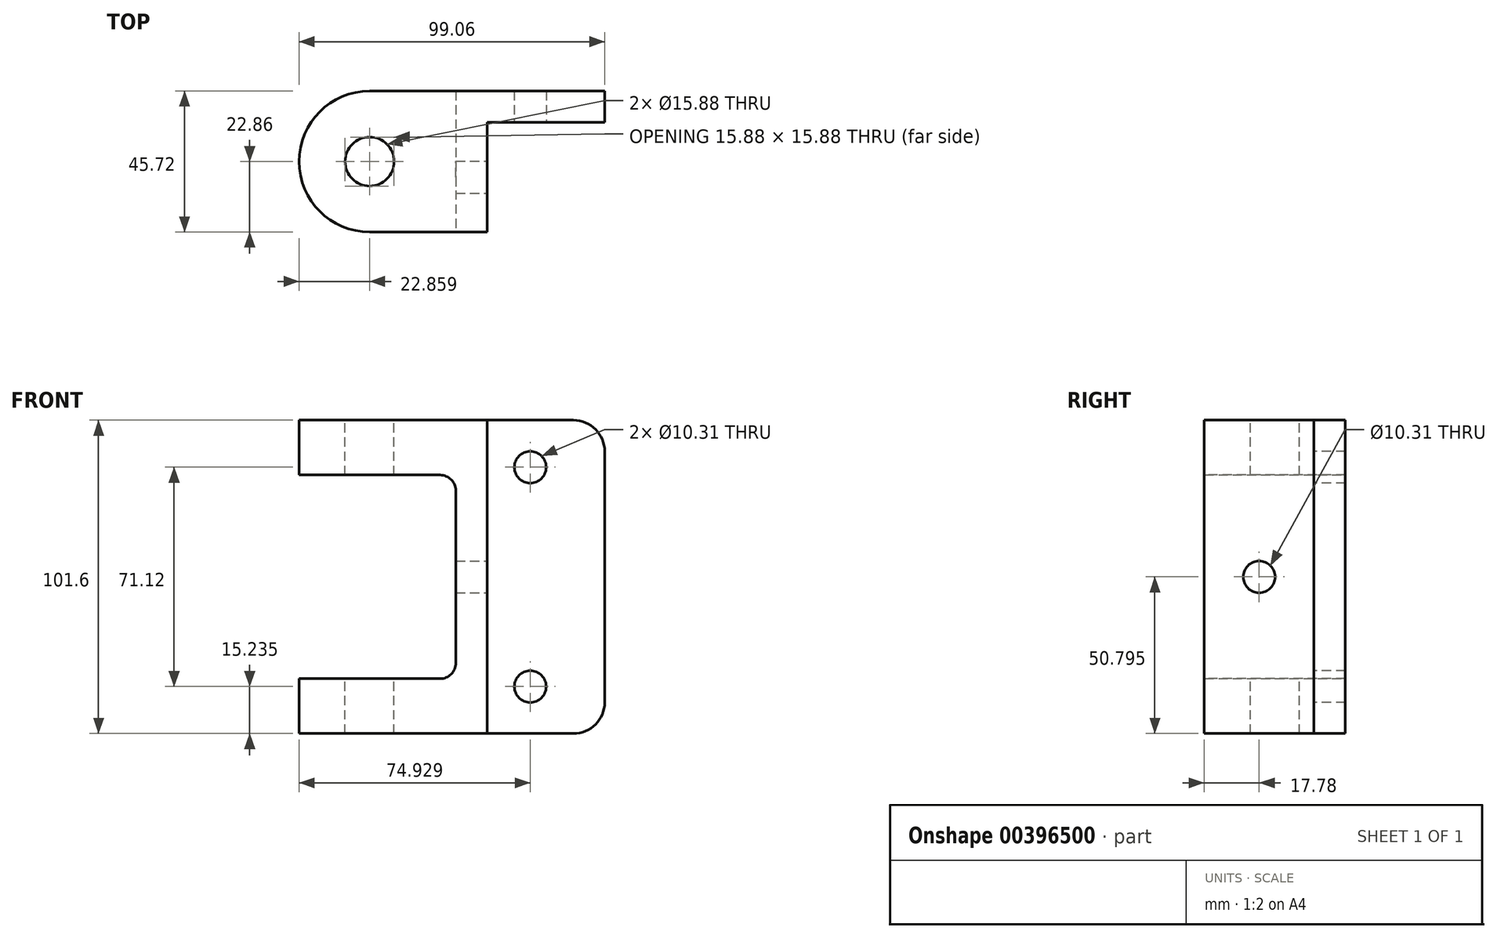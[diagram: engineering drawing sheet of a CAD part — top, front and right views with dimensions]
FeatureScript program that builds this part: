
annotation { "Feature Type Name" : "Feature", "Feature Type Description" : "" }
export const myFeature = defineFeature(function(context is Context, id is Id, definition is map)
    precondition{}
    {
        {
            var Q0;
            Q0=qCreatedBy(makeId("Front.planeOp"),FACE);
            var sketch = newSketch(context, id + "F0", { "sketchPlane" : qUnion([Q0])});
            skLineSegment(sketch, "E0.bottom", {"start": v(-44.01, 40.62) * mm, "end": v(55.05, 40.62) * mm});
            skLineSegment(sketch, "E0.top", {"start": v(-44.01, -60.98) * mm, "end": v(55.05, -60.98) * mm});
            skLineSegment(sketch, "E0.left", {"start": v(-44.01, 40.62) * mm, "end": v(-44.01, -60.98) * mm});
            skLineSegment(sketch, "E0.right", {"start": v(55.05, 40.62) * mm, "end": v(55.05, -60.98) * mm});
            skSolve(sketch);
        }
        {
            var Q0;
            Q0=makeQuery(id+"F0.imprint","IMPRINT",FACE,{"disambiguationData":[TD([[makeQuery(id+"F0.imprint","IMPRINT",EDGE,{"derivedFrom":sQuery(id+"F0.wireOp",EDGE,"E0.bottom")}),-1.0]])]});
            extrude(context, id + "F1", {"entities" : qUnion([Q0]), "depth" : 45.72 * mm});
        }
        {
            var Q0;
            Q0=makeQuery(id+"F1.opExtrude","CAP_FACE",FACE,{"disambiguationData":[OSD([sQuery(id+"F0.wireOp",EDGE,"E0.bottom"),sQuery(id+"F0.wireOp",EDGE,"E0.top"),sQuery(id+"F0.wireOp",EDGE,"E0.left"),sQuery(id+"F0.wireOp",EDGE,"E0.right")])],"isStart":false});
            var sketch = newSketch(context, id + "F2", { "sketchPlane" : qUnion([Q0])});
            skLineSegment(sketch, "E1.bottom", {"start": v(16.95, 43.76) * mm, "end": v(62.8, 43.76) * mm});
            skLineSegment(sketch, "E1.top", {"start": v(16.95, -63.37) * mm, "end": v(62.8, -63.37) * mm});
            skLineSegment(sketch, "E1.left", {"start": v(16.95, 43.76) * mm, "end": v(16.95, -63.37) * mm});
            skLineSegment(sketch, "E1.right", {"start": v(62.8, 43.76) * mm, "end": v(62.8, -63.37) * mm});
            skSolve(sketch);
        }
        {
            var Q0;
            Q0 = qSketchRegion(id + "F2", true);
            extrude(context, id + "F3", {"entities" : qUnion([Q0]), "operationType" : NewBodyOperationType.REMOVE, "oppositeDirection" : true, "depth" : 35.56 * mm});
        }
        {
            var Q0;
            Q0=makeQuery(id+"F1.opExtrude","CAP_FACE",FACE,{"disambiguationData":[OSD([sQuery(id+"F0.wireOp",EDGE,"E0.bottom"),sQuery(id+"F0.wireOp",EDGE,"E0.top"),sQuery(id+"F0.wireOp",EDGE,"E0.left"),sQuery(id+"F0.wireOp",EDGE,"E0.right")])],"isStart":false});
            var sketch = newSketch(context, id + "F4", { "sketchPlane" : qUnion([Q0])});
            skLineSegment(sketch, "E2.bottom", {"start": v(-89.68, 22.84) * mm, "end": v(6.79, 22.84) * mm});
            skLineSegment(sketch, "E2.top", {"start": v(-89.68, -43.2) * mm, "end": v(6.79, -43.2) * mm});
            skLineSegment(sketch, "E2.left", {"start": v(-89.68, 22.84) * mm, "end": v(-89.68, -43.2) * mm});
            skLineSegment(sketch, "E2.right", {"start": v(6.79, 22.84) * mm, "end": v(6.79, -43.2) * mm});
            skSolve(sketch);
        }
        {
            var Q0;
            Q0 = qSketchRegion(id + "F4", true);
            extrude(context, id + "F5", {"entities" : qUnion([Q0]), "operationType" : NewBodyOperationType.REMOVE, "endBound" : BoundingType.THROUGH_ALL, "oppositeDirection" : true, "depth" : 25.4 * mm});
        }
        {
            var Q0;
            {var subQ0=sQuery(id+"F0.wireOp",EDGE,"E0.bottom");var subQ1=sQuery(id+"F0.wireOp",EDGE,"E0.left");Q0=makeQuery(id+"F5.boolean.opBoolean","SPLIT",EDGE,{"disambiguationData":[TD([makeQuery(id+"F1.opExtrude","SWEPT_FACE",FACE,{"disambiguationData":[OSD([subQ0])]})])],"derivedFrom":makeQuery(id+"F1.opExtrude","CAP_EDGE",EDGE,{"disambiguationData":[OSD([subQ1])],"isStart":true})});}
            var Q1;
            {var subQ0=sQuery(id+"F0.wireOp",EDGE,"E0.bottom");var subQ1=sQuery(id+"F0.wireOp",EDGE,"E0.left");Q1=makeQuery(id+"F5.boolean.opBoolean","SPLIT",EDGE,{"disambiguationData":[TD([makeQuery(id+"F1.opExtrude","SWEPT_FACE",FACE,{"disambiguationData":[OSD([subQ0])]})])],"derivedFrom":makeQuery(id+"F1.opExtrude","CAP_EDGE",EDGE,{"disambiguationData":[OSD([subQ1])],"isStart":false})});}
            var Q2;
            {var subQ0=sQuery(id+"F0.wireOp",EDGE,"E0.left");var subQ1=sQuery(id+"F0.wireOp",EDGE,"E0.top");Q2=makeQuery(id+"F5.boolean.opBoolean","SPLIT",EDGE,{"disambiguationData":[TD([makeQuery(id+"F1.opExtrude","SWEPT_FACE",FACE,{"disambiguationData":[OSD([subQ1])]})])],"derivedFrom":makeQuery(id+"F1.opExtrude","CAP_EDGE",EDGE,{"disambiguationData":[OSD([subQ0])],"isStart":true})});}
            var Q3;
            {var subQ0=sQuery(id+"F0.wireOp",EDGE,"E0.left");var subQ1=sQuery(id+"F0.wireOp",EDGE,"E0.top");Q3=makeQuery(id+"F5.boolean.opBoolean","SPLIT",EDGE,{"disambiguationData":[TD([makeQuery(id+"F1.opExtrude","SWEPT_FACE",FACE,{"disambiguationData":[OSD([subQ1])]})])],"derivedFrom":makeQuery(id+"F1.opExtrude","CAP_EDGE",EDGE,{"disambiguationData":[OSD([subQ0])],"isStart":false})});}
            fillet(context, id + "F6", {"entities" : qUnion([Q0, Q1, Q2, Q3]), "radius" : 22.86 * mm, "tangentPropagation" : true, "allowEdgeOverflow" : false});
        }
        {
            var Q0;
            Q0=makeQuery(id+"F1.opExtrude","SWEPT_FACE",FACE,{"disambiguationData":[OSD([sQuery(id+"F0.wireOp",EDGE,"E0.bottom")])]});
            var sketch = newSketch(context, id + "F7", { "sketchPlane" : qUnion([Q0])});
            skCircle(sketch, "E3", {"center": v(-21.15, -22.86) * mm, "radius": 7.94 * mm});
            skSolve(sketch);
        }
        {
            var Q0;
            Q0 = qSketchRegion(id + "F7", true);
            extrude(context, id + "F8", {"entities" : qUnion([Q0]), "operationType" : NewBodyOperationType.REMOVE, "endBound" : BoundingType.THROUGH_ALL, "oppositeDirection" : true, "depth" : 25.4 * mm});
        }
        {
            var Q0;
            Q0=makeQuery(id+"F5.boolean.opBoolean","COPY",EDGE,{"derivedFrom":makeQuery(id+"F5.opExtrude","SWEPT_EDGE",EDGE,{"disambiguationData":[OSD([sQuery(id+"F4.wireOp",EDGE,"E2.bottom"),sQuery(id+"F4.wireOp",EDGE,"E2.right")])]})});
            var Q1;
            Q1=makeQuery(id+"F5.boolean.opBoolean","COPY",EDGE,{"derivedFrom":makeQuery(id+"F5.opExtrude","SWEPT_EDGE",EDGE,{"disambiguationData":[OSD([sQuery(id+"F4.wireOp",EDGE,"E2.top"),sQuery(id+"F4.wireOp",EDGE,"E2.right")])]})});
            fillet(context, id + "F9", {"entities" : qUnion([Q0, Q1]), "radius" : 5.08 * mm, "tangentPropagation" : true, "allowEdgeOverflow" : false});
        }
        {
            var Q0;
            Q0=makeQuery(id+"F1.opExtrude","SWEPT_EDGE",EDGE,{"disambiguationData":[OSD([sQuery(id+"F0.wireOp",EDGE,"E0.bottom"),sQuery(id+"F0.wireOp",EDGE,"E0.right")])]});
            var Q1;
            Q1=makeQuery(id+"F1.opExtrude","SWEPT_EDGE",EDGE,{"disambiguationData":[OSD([sQuery(id+"F0.wireOp",EDGE,"E0.top"),sQuery(id+"F0.wireOp",EDGE,"E0.right")])]});
            fillet(context, id + "F10", {"entities" : qUnion([Q0, Q1]), "radius" : 10.16 * mm, "tangentPropagation" : true, "allowEdgeOverflow" : false});
        }
        {
            var Q0;
            Q0=makeQuery(id+"F3.boolean.opBoolean","COPY",FACE,{"derivedFrom":makeQuery(id+"F3.opExtrude","SWEPT_FACE",FACE,{"disambiguationData":[OSD([sQuery(id+"F2.wireOp",EDGE,"E1.left")])]})});
            var sketch = newSketch(context, id + "F11", { "sketchPlane" : qUnion([Q0])});
            skCircle(sketch, "E4", {"center": v(-27.94, -10.18) * mm, "radius": 5.16 * mm});
            skPoint(sketch, "E4.centerSnap0", {"position": v(-27.94, 40.62) * mm});
            skPoint(sketch, "E4.centerSnap1", {"position": v(-45.72, -10.18) * mm});
            skSolve(sketch);
        }
        {
            var Q0;
            Q0 = qSketchRegion(id + "F11", true);
            extrude(context, id + "F12", {"entities" : qUnion([Q0]), "operationType" : NewBodyOperationType.REMOVE, "endBound" : BoundingType.THROUGH_ALL, "oppositeDirection" : true, "depth" : 25.4 * mm});
        }
        {
            var Q0;
            Q0=makeQuery(id+"F3.boolean.opBoolean","COPY",FACE,{"derivedFrom":makeQuery(id+"F3.opExtrude","CAP_FACE",FACE,{"disambiguationData":[OSD([sQuery(id+"F2.wireOp",EDGE,"E1.bottom"),sQuery(id+"F2.wireOp",EDGE,"E1.top"),sQuery(id+"F2.wireOp",EDGE,"E1.left"),sQuery(id+"F2.wireOp",EDGE,"E1.right")])],"isStart":false})});
            var sketch = newSketch(context, id + "F13", { "sketchPlane" : qUnion([Q0])});
            skCircle(sketch, "E5", {"center": v(30.92, 25.38) * mm, "radius": 5.16 * mm});
            skPoint(sketch, "E5.centerSnap0", {"position": v(30.92, 40.62) * mm});
            skCircle(sketch, "E6", {"center": v(30.92, -45.74) * mm, "radius": 5.16 * mm});
            skPoint(sketch, "E6.centerSnap0", {"position": v(30.92, -60.98) * mm});
            skSolve(sketch);
        }
        {
            var Q0;
            Q0 = qSketchRegion(id + "F13", true);
            extrude(context, id + "F14", {"entities" : qUnion([Q0]), "operationType" : NewBodyOperationType.REMOVE, "endBound" : BoundingType.THROUGH_ALL, "oppositeDirection" : true, "depth" : 25.4 * mm});
        }
    });
